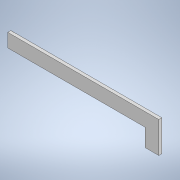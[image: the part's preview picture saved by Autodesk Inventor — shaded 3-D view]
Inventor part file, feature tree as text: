
AUTODESK INVENTOR PART (.ipt)
format: ipt  version: 2022 (Build 260153000, 153)  size: 125,440 bytes
history: native  units: mm
features: extrude x3, sketch x2, fillet x1, projected_geometry x1
ambient origin geometry x8: Origin, YZ Plane, XZ Plane, XY Plane, X Axis, Y Axis, Z Axis, Center Point
bodies: Solid1 (feature_tree)
feature tree (7):
  sketch  "Sketch1"  dims[d0=132.5mm d1=10.0mm]
  extrude  "Extrusion1"  Depth=10.0mm
  extrude  "Extrusion2"  Depth=20.0mm
  extrude  "Extrusion3"  Depth=3.0mm
  fillet  "Fillet1"  Radius=3.0mm
  sketch  "Sketch2"  dims[d2=10.0mm d3=20.0mm d4=3.0mm d5=3.0mm d6=3.0mm d7=0.0mm d8=10.0mm d9=0.0mm d10=2.0mm d11=3.0mm d12=0.0mm]
  projected_geometry  "Projected Loop1"
